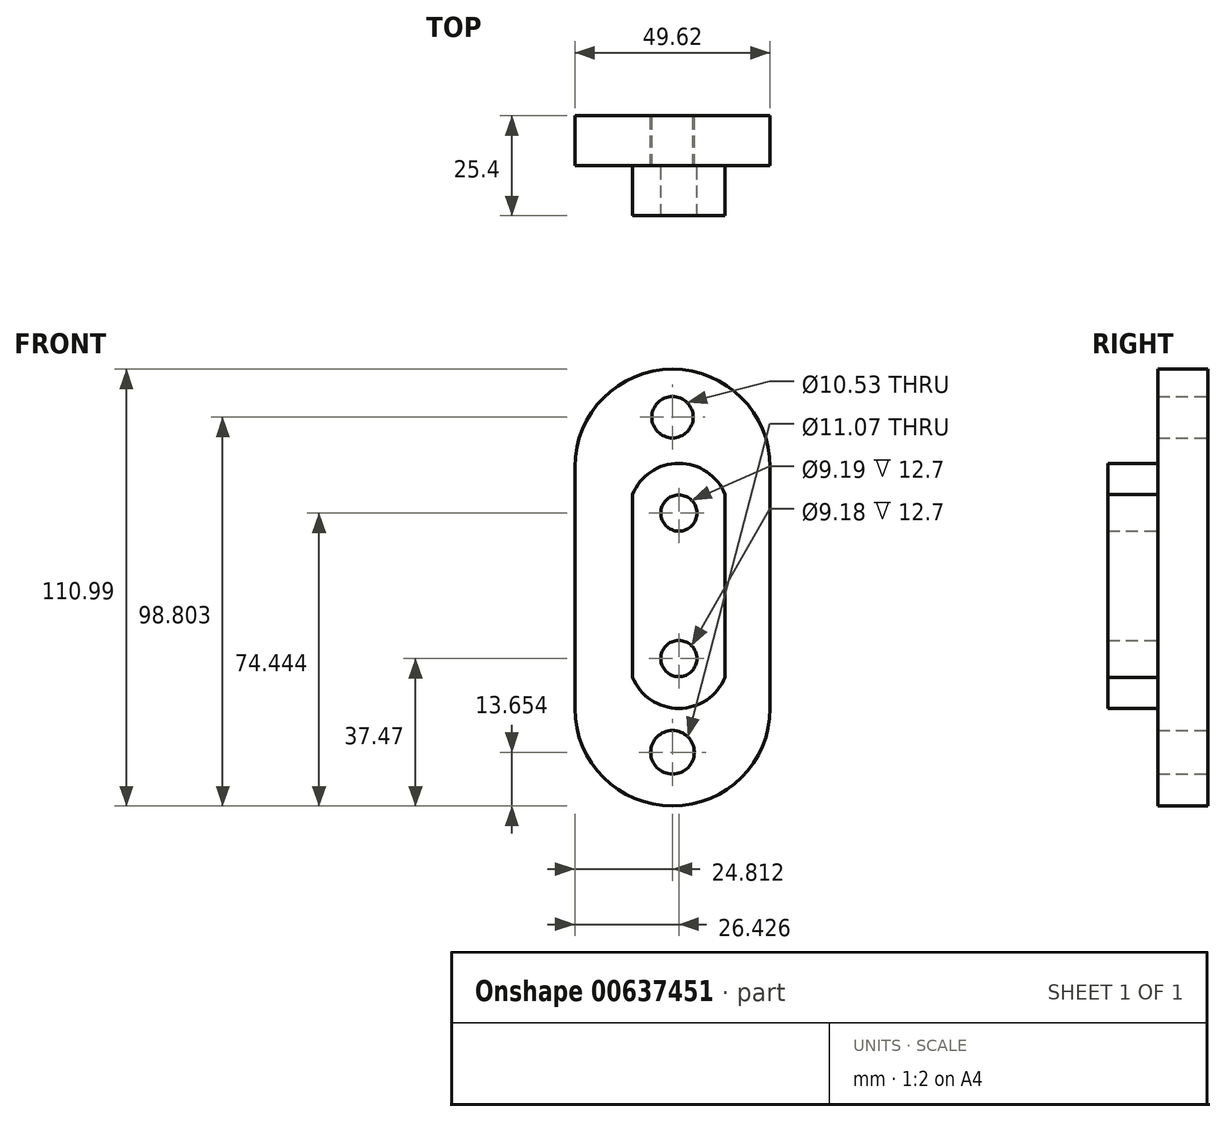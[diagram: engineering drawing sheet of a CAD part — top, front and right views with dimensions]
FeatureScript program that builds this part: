
annotation { "Feature Type Name" : "Feature", "Feature Type Description" : "" }
export const myFeature = defineFeature(function(context is Context, id is Id, definition is map)
    precondition{}
    {
        {
            var Q0;
            Q0=qCreatedBy(makeId("Front.planeOp"),FACE);
            var sketch = newSketch(context, id + "F0", { "sketchPlane" : qUnion([Q0])});
            skLineSegment(sketch, "E0", {"start": v(-33.62, 24.96) * mm, "end": v(-33.62, -36.4) * mm});
            skLineSegment(sketch, "E1", {"start": v(16, -36.4) * mm, "end": v(16, 24.96) * mm});
            skArc(sketch, "E2", {"start": v(16, 24.96) * mm, "mid": v(-8.8, 49.77) * mm, "end": v(-33.62, 24.96) * mm});
            skArc(sketch, "E3", {"start": v(-33.62, -36.4) * mm, "mid": v(-8.8, -61.22) * mm, "end": v(16, -36.4) * mm});
            skCircle(sketch, "E4", {"center": v(-8.8, 37.58) * mm, "radius": 5.26 * mm});
            skCircle(sketch, "E5", {"center": v(-8.8, -47.57) * mm, "radius": 5.53 * mm});
            skSolve(sketch);
        }
        {
            var Q0;
            Q0 = qSketchRegion(id + "F0", true);
            extrude(context, id + "F1", {"entities" : qUnion([Q0]), "depth" : 12.7 * mm, "offsetDistance" : 25.4 * mm});
        }
        {
            var Q0;
            Q0=qCreatedBy(makeId("Front.planeOp"),FACE);
            var sketch = newSketch(context, id + "F2", { "sketchPlane" : qUnion([Q0])});
            skLineSegment(sketch, "E6.left", {"start": v(-18.94, 17.91) * mm, "end": v(-18.94, -28.48) * mm});
            skLineSegment(sketch, "E6.right", {"start": v(4.55, 17.91) * mm, "end": v(4.55, -28.48) * mm});
            skArc(sketch, "E7", {"start": v(4.55, 17.91) * mm, "mid": v(-7.2, 25.87) * mm, "end": v(-18.94, 17.91) * mm});
            skArc(sketch, "E8", {"start": v(-18.94, -28.48) * mm, "mid": v(-7.2, -36.41) * mm, "end": v(4.55, -28.48) * mm});
            skCircle(sketch, "E9", {"center": v(-7.2, 13.22) * mm, "radius": 4.6 * mm});
            skCircle(sketch, "E10", {"center": v(-7.2, -23.75) * mm, "radius": 4.6 * mm});
            skSolve(sketch);
        }
        {
            var Q0;
            Q0 = qSketchRegion(id + "F2", true);
            extrude(context, id + "F3", {"entities" : qUnion([Q0]), "operationType" : NewBodyOperationType.ADD, "depth" : 25.4 * mm, "offsetDistance" : 25.4 * mm});
        }
    });
